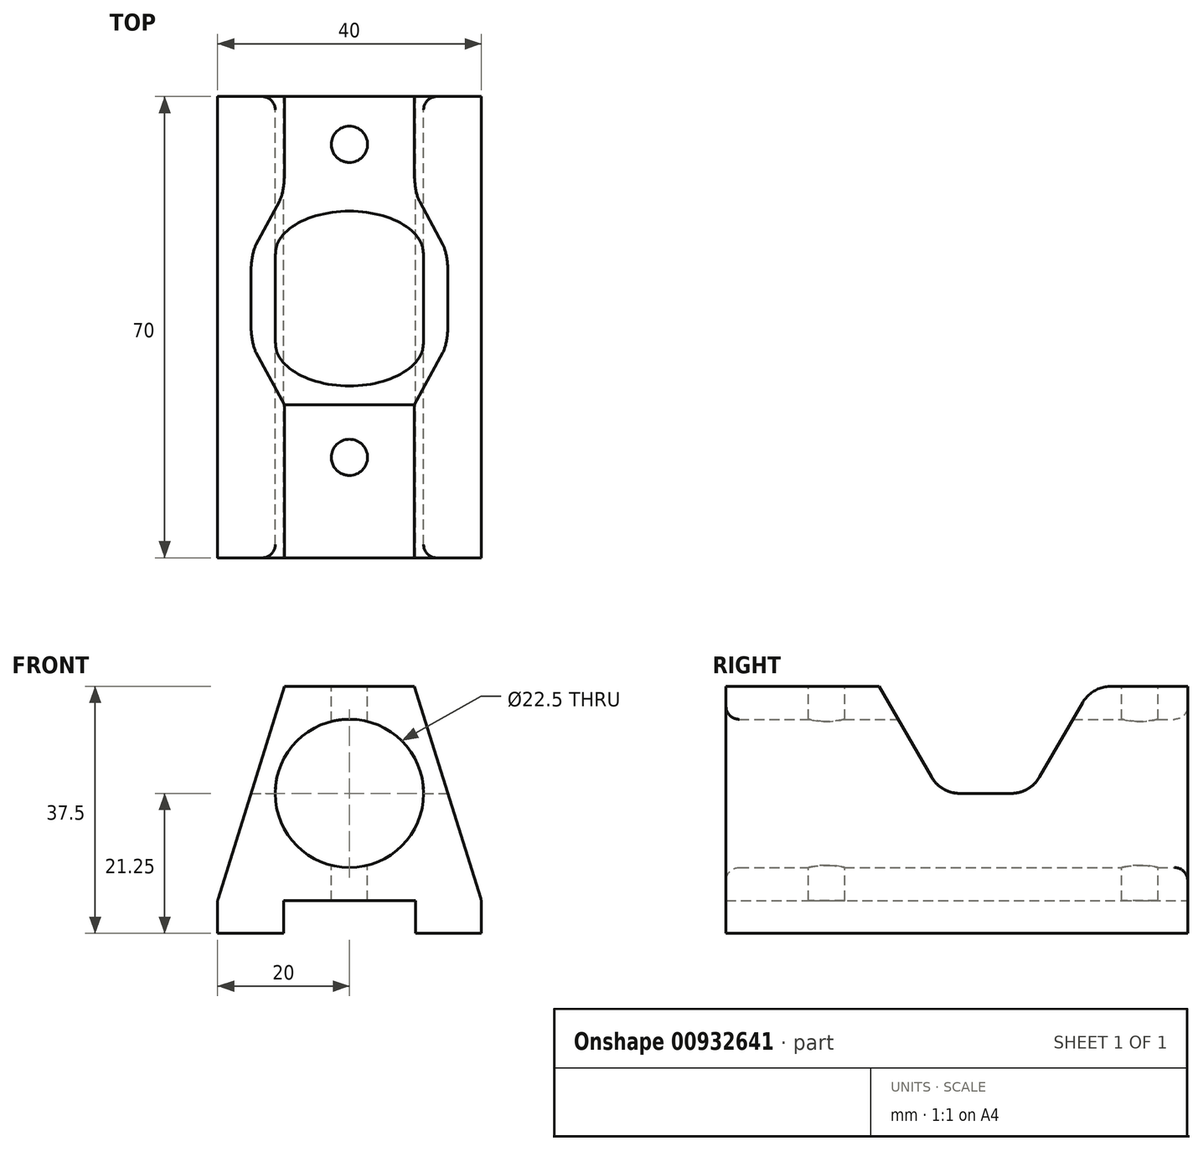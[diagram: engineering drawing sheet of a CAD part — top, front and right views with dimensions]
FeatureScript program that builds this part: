
annotation { "Feature Type Name" : "Feature", "Feature Type Description" : "" }
export const myFeature = defineFeature(function(context is Context, id is Id, definition is map)
    precondition{}
    {
        {
            var Q0;
            Q0=qCreatedBy(makeId("Front.planeOp"),FACE);
            var sketch = newSketch(context, id + "F0", { "sketchPlane" : qUnion([Q0])});
            skCircle(sketch, "E0", {"center": v(0, 0) * mm, "radius": 11.25 * mm});
            skLineSegment(sketch, "E1", {"start": v(0, 16.25) * mm, "end": v(-9.86, 16.25) * mm});
            skLineSegment(sketch, "E2", {"start": v(-9.86, 16.25) * mm, "end": v(-20, -16.25) * mm});
            skLineSegment(sketch, "E3", {"start": v(-20, -16.25) * mm, "end": v(0, -16.25) * mm});
            skLineSegment(sketch, "E4", {"start": v(0, -16.25) * mm, "end": v(0, 30.6) * mm, "construction": true});
            skLineSegment(sketch, "E5.MirrorCS", {"start": v(0, 16.25) * mm, "end": v(9.86, 16.25) * mm});
            skLineSegment(sketch, "E6.MirrorCS", {"start": v(9.86, 16.25) * mm, "end": v(20, -16.25) * mm});
            skLineSegment(sketch, "E7.MirrorCS", {"start": v(20, -16.25) * mm, "end": v(0, -16.25) * mm});
            skSolve(sketch);
        }
        {
            var Q0;
            Q0 = qSketchRegion(id + "F0", true);
            extrude(context, id + "F1", {"entities" : qUnion([Q0]), "depth" : 60 * mm, "offsetDistance" : 25 * mm});
        }
        {
            var Q0;
            Q0=makeQuery(id+"F1.opExtrude","CAP_FACE",FACE,{"disambiguationData":[OSD([sQuery(id+"F0.wireOp",EDGE,"E0"),sQuery(id+"F0.wireOp",EDGE,"E1"),sQuery(id+"F0.wireOp",EDGE,"E2"),sQuery(id+"F0.wireOp",EDGE,"E3"),sQuery(id+"F0.wireOp",EDGE,"E5.MirrorCS"),sQuery(id+"F0.wireOp",EDGE,"E6.MirrorCS"),sQuery(id+"F0.wireOp",EDGE,"E7.MirrorCS")])],"isStart":true});
            var sketch = newSketch(context, id + "F2", { "sketchPlane" : qUnion([Q0])});
            skLineSegment(sketch, "E8.0", {"start": v(-9.86, 16.25) * mm, "end": v(-20, -16.25) * mm});
            skLineSegment(sketch, "E9.0", {"start": v(9.86, 16.25) * mm, "end": v(-9.86, 16.25) * mm});
            skLineSegment(sketch, "E10.0", {"start": v(9.86, 16.25) * mm, "end": v(20, -16.25) * mm});
            skLineSegment(sketch, "E11.0", {"start": v(-20, -16.25) * mm, "end": v(20, -16.25) * mm});
            skCircle(sketch, "E12.0", {"center": v(0, 0) * mm, "radius": 11.25 * mm});
            skSolve(sketch);
        }
        {
            var Q0;
            Q0 = qSketchRegion(id + "F2", true);
            extrude(context, id + "F3", {"entities" : qUnion([Q0]), "operationType" : NewBodyOperationType.ADD, "depth" : 10 * mm, "offsetDistance" : 25 * mm});
        }
        {
            var Q0;
            Q0=makeQuery(id+"F1.opExtrude","SWEPT_FACE",FACE,{"disambiguationData":[OSD([sQuery(id+"F0.wireOp",EDGE,"E1"),sQuery(id+"F0.wireOp",EDGE,"E5.MirrorCS")])]});
            var sketch = newSketch(context, id + "F4", { "sketchPlane" : qUnion([Q0])});
            skCircle(sketch, "E13", {"center": v(0, -44.75) * mm, "radius": 2.75 * mm});
            skCircle(sketch, "E14", {"center": v(0, 2.75) * mm, "radius": 2.75 * mm});
            skSolve(sketch);
        }
        {
            var Q0;
            Q0 = qSketchRegion(id + "F4", true);
            extrude(context, id + "F5", {"entities" : qUnion([Q0]), "operationType" : NewBodyOperationType.REMOVE, "endBound" : BoundingType.THROUGH_ALL, "oppositeDirection" : true, "depth" : 25 * mm, "offsetDistance" : 25 * mm});
        }
        {
            var Q0;
            Q0=makeQuery(id+"F3.boolean.opBoolean","MERGE",FACE,{"derivedFrom":[makeQuery(id+"F1.opExtrude","SWEPT_FACE",FACE,{"disambiguationData":[OSD([sQuery(id+"F0.wireOp",EDGE,"E3"),sQuery(id+"F0.wireOp",EDGE,"E7.MirrorCS")])]}),makeQuery(id+"F3.opExtrude","SWEPT_FACE",FACE,{"disambiguationData":[OSD([sQuery(id+"F2.wireOp",EDGE,"E11.0")])]})]});
            var sketch = newSketch(context, id + "F6", { "sketchPlane" : qUnion([Q0])});
            skLineSegment(sketch, "E15", {"start": v(0, 44.75) * mm, "end": v(0, -2.75) * mm, "construction": true});
            skLineSegment(sketch, "E16.bottom", {"start": v(20, 60) * mm, "end": v(10, 60) * mm});
            skLineSegment(sketch, "E16.top", {"start": v(20, -10) * mm, "end": v(10, -10) * mm});
            skLineSegment(sketch, "E16.left", {"start": v(20, 60) * mm, "end": v(20, -10) * mm});
            skLineSegment(sketch, "E16.right", {"start": v(10, 60) * mm, "end": v(10, -10) * mm});
            skLineSegment(sketch, "E17.MirrorCS", {"start": v(-10, 60) * mm, "end": v(-10, -10) * mm});
            skLineSegment(sketch, "E18.MirrorCS", {"start": v(-20, 60) * mm, "end": v(-10, 60) * mm});
            skLineSegment(sketch, "E19.MirrorCS", {"start": v(-20, 60) * mm, "end": v(-20, -10) * mm});
            skLineSegment(sketch, "E20.MirrorCS", {"start": v(-20, -10) * mm, "end": v(-10, -10) * mm});
            skSolve(sketch);
        }
        {
            var Q0;
            Q0 = qSketchRegion(id + "F6", true);
            extrude(context, id + "F7", {"entities" : qUnion([Q0]), "operationType" : NewBodyOperationType.ADD, "depth" : 5 * mm, "offsetDistance" : 25 * mm});
        }
        {
            var Q0;
            Q0=qCreatedBy(makeId("Right.planeOp"),FACE);
            var sketch = newSketch(context, id + "F8", { "sketchPlane" : qUnion([Q0])});
            skLineSegment(sketch, "E21", {"start": v(-4.5, 16.25) * mm, "end": v(-13.88, 0) * mm});
            skLineSegment(sketch, "E22", {"start": v(-13.88, 0) * mm, "end": v(-27.42, 0) * mm});
            skLineSegment(sketch, "E23", {"start": v(-27.42, 0) * mm, "end": v(-36.8, 16.25) * mm});
            skLineSegment(sketch, "E24", {"start": v(-4.5, 16.25) * mm, "end": v(-36.8, 16.25) * mm});
            skLineSegment(sketch, "E25.0", {"start": v(0, 16.25) * mm, "end": v(5.5, 16.25) * mm, "construction": true});
            skLineSegment(sketch, "E26.0", {"start": v(-47.5, 16.25) * mm, "end": v(-42, 16.25) * mm, "construction": true});
            skSolve(sketch);
        }
        {
            var Q0;
            Q0 = qSketchRegion(id + "F8", true);
            extrude(context, id + "F9", {"entities" : qUnion([Q0]), "operationType" : NewBodyOperationType.REMOVE, "endBound" : BoundingType.THROUGH_ALL, "oppositeDirection" : true, "depth" : 25 * mm, "offsetDistance" : 25 * mm, "hasSecondDirection" : true, "secondDirectionBound" : SecondDirectionBoundingType.THROUGH_ALL, "secondDirectionOppositeDirection" : false, "secondDirectionDepth" : 25 * mm});
        }
        {
            var Q0;
            {var subQ0=sQuery(id+"F8.wireOp",EDGE,"E21");var subQ1=sQuery(id+"F8.wireOp",EDGE,"E22");Q0=makeQuery(id+"F9.boolean.opBoolean","COPY",EDGE,{"disambiguationData":[TD([makeQuery(id+"F1.opExtrude","SWEPT_FACE",FACE,{"disambiguationData":[OSD([sQuery(id+"F0.wireOp",EDGE,"E2")])]})])],"derivedFrom":makeQuery(id+"F9.opExtrude","SWEPT_EDGE",EDGE,{"disambiguationData":[OSD([subQ0,subQ1])]})});}
            var Q1;
            {var subQ0=sQuery(id+"F8.wireOp",EDGE,"E22");var subQ1=sQuery(id+"F8.wireOp",EDGE,"E21");Q1=makeQuery(id+"F9.boolean.opBoolean","COPY",EDGE,{"disambiguationData":[TD([makeQuery(id+"F1.opExtrude","SWEPT_FACE",FACE,{"disambiguationData":[OSD([sQuery(id+"F0.wireOp",EDGE,"E6.MirrorCS")])]})])],"derivedFrom":makeQuery(id+"F9.opExtrude","SWEPT_EDGE",EDGE,{"disambiguationData":[OSD([subQ1,subQ0])]})});}
            var Q2;
            {var subQ0=sQuery(id+"F8.wireOp",EDGE,"E22");var subQ1=sQuery(id+"F8.wireOp",EDGE,"E23");Q2=makeQuery(id+"F9.boolean.opBoolean","COPY",EDGE,{"disambiguationData":[TD([makeQuery(id+"F1.opExtrude","SWEPT_FACE",FACE,{"disambiguationData":[OSD([sQuery(id+"F0.wireOp",EDGE,"E6.MirrorCS")])]})])],"derivedFrom":makeQuery(id+"F9.opExtrude","SWEPT_EDGE",EDGE,{"disambiguationData":[OSD([subQ0,subQ1])]})});}
            var Q3;
            {var subQ0=sQuery(id+"F8.wireOp",EDGE,"E22");var subQ1=sQuery(id+"F8.wireOp",EDGE,"E23");Q3=makeQuery(id+"F9.boolean.opBoolean","COPY",EDGE,{"disambiguationData":[TD([makeQuery(id+"F1.opExtrude","SWEPT_FACE",FACE,{"disambiguationData":[OSD([sQuery(id+"F0.wireOp",EDGE,"E2")])]})])],"derivedFrom":makeQuery(id+"F9.opExtrude","SWEPT_EDGE",EDGE,{"disambiguationData":[OSD([subQ0,subQ1])]})});}
            var Q4;
            Q4=makeQuery(id+"F9.boolean.opBoolean","COPY",EDGE,{"derivedFrom":makeQuery(id+"F9.opExtrude","SWEPT_EDGE",EDGE,{"disambiguationData":[OSD([sQuery(id+"F8.wireOp",EDGE,"E23"),sQuery(id+"F8.wireOp",EDGE,"E24")])]})});
            var Q5;
            Q5=makeQuery(id+"F9.boolean.opBoolean","COPY",EDGE,{"derivedFrom":makeQuery(id+"F9.opExtrude","SWEPT_EDGE",EDGE,{"disambiguationData":[OSD([sQuery(id+"F8.wireOp",EDGE,"E21"),sQuery(id+"F8.wireOp",EDGE,"E24")])]})});
            fillet(context, id + "F10", {"entities" : qUnion([Q0, Q1, Q2, Q3, Q4, Q5]), "radius" : 5 * mm, "tangentPropagation" : true, "allowEdgeOverflow" : false});
        }
        {
            var Q0;
            Q0=makeQuery(id+"F3.opExtrude","CAP_EDGE",EDGE,{"disambiguationData":[OSD([sQuery(id+"F2.wireOp",EDGE,"E12.0")])],"isStart":false});
            var Q1;
            Q1=makeQuery(id+"F1.opExtrude","CAP_EDGE",EDGE,{"disambiguationData":[OSD([sQuery(id+"F0.wireOp",EDGE,"E0")])],"isStart":false});
            var Q2;
            Q2=makeQuery(id+"F7.boolean.opBoolean","MERGE",EDGE,{"derivedFrom":[makeQuery(id+"F3.boolean.opBoolean","MERGE",EDGE,{"derivedFrom":[makeQuery(id+"F1.opExtrude","SWEPT_EDGE",EDGE,{"disambiguationData":[OSD([sQuery(id+"F0.wireOp",EDGE,"E2"),sQuery(id+"F0.wireOp",EDGE,"E3")])]}),makeQuery(id+"F3.opExtrude","SWEPT_EDGE",EDGE,{"disambiguationData":[OSD([sQuery(id+"F2.wireOp",EDGE,"E10.0"),sQuery(id+"F2.wireOp",EDGE,"E11.0")])]})]}),makeQuery(id+"F7.opExtrude","CAP_EDGE",EDGE,{"disambiguationData":[OSD([sQuery(id+"F6.wireOp",EDGE,"E19.MirrorCS")])],"isStart":true})]});
            var Q3;
            Q3=makeQuery(id+"F7.boolean.opBoolean","MERGE",EDGE,{"derivedFrom":[makeQuery(id+"F3.boolean.opBoolean","MERGE",EDGE,{"derivedFrom":[makeQuery(id+"F1.opExtrude","SWEPT_EDGE",EDGE,{"disambiguationData":[OSD([sQuery(id+"F0.wireOp",EDGE,"E6.MirrorCS"),sQuery(id+"F0.wireOp",EDGE,"E7.MirrorCS")])]}),makeQuery(id+"F3.opExtrude","SWEPT_EDGE",EDGE,{"disambiguationData":[OSD([sQuery(id+"F2.wireOp",EDGE,"E8.0"),sQuery(id+"F2.wireOp",EDGE,"E11.0")])]})]}),makeQuery(id+"F7.opExtrude","CAP_EDGE",EDGE,{"disambiguationData":[OSD([sQuery(id+"F6.wireOp",EDGE,"E16.left")])],"isStart":true})]});
            var Q4;
            Q4=makeQuery(id+"F7.opExtrude","CAP_EDGE",EDGE,{"disambiguationData":[OSD([sQuery(id+"F6.wireOp",EDGE,"E17.MirrorCS")])],"isStart":true});
            var Q5;
            Q5=makeQuery(id+"F7.opExtrude","CAP_EDGE",EDGE,{"disambiguationData":[OSD([sQuery(id+"F6.wireOp",EDGE,"E16.right")])],"isStart":true});
            fillet(context, id + "F11", {"entities" : qUnion([Q0, Q1, Q2, Q3, Q4, Q5]), "radius" : 2 * mm, "tangentPropagation" : true, "allowEdgeOverflow" : false});
        }
    });
